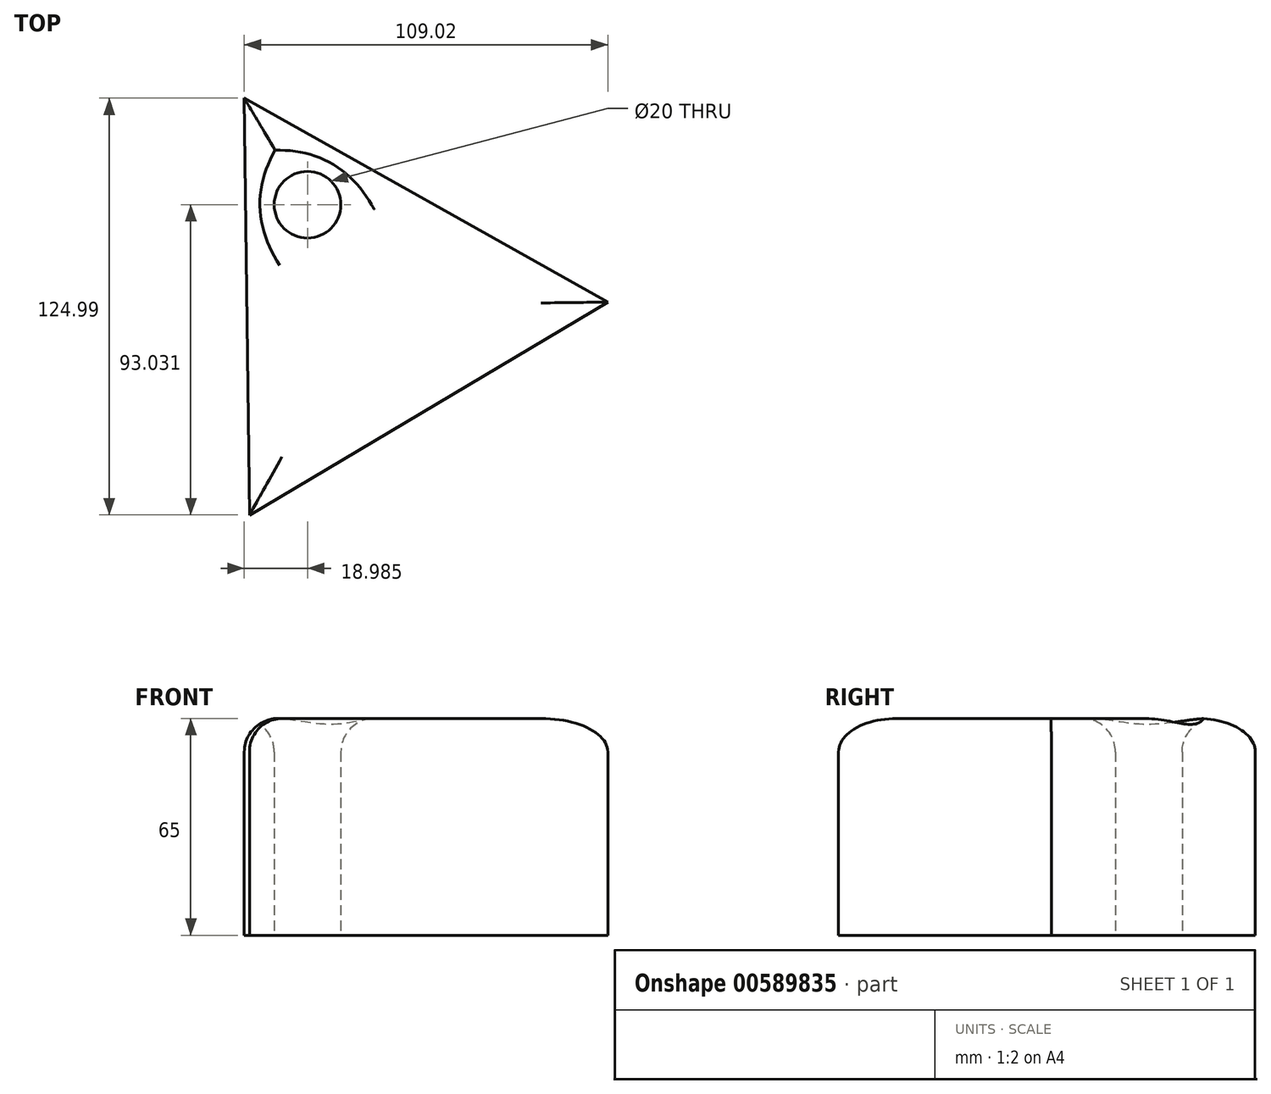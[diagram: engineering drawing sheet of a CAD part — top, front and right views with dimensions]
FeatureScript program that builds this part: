
annotation { "Feature Type Name" : "Feature", "Feature Type Description" : "" }
export const myFeature = defineFeature(function(context is Context, id is Id, definition is map)
    precondition{}
    {
        {
            var Q0;
            Q0=qCreatedBy(makeId("Top.planeOp"),FACE);
            var sketch = newSketch(context, id + "F0", { "sketchPlane" : qUnion([Q0])});
            skCircle(sketch, "E0.cCircle", {"center": v(0, 0) * mm, "radius": 36.08 * mm, "construction": true});
            skLineSegment(sketch, "E0.0", {"start": v(72.16, 0.9) * mm, "end": v(-35.3, -62.94) * mm});
            skLineSegment(sketch, "E0.1", {"start": v(-35.3, -62.94) * mm, "end": v(-36.86, 62.05) * mm});
            skLineSegment(sketch, "E0.2", {"start": v(-36.86, 62.05) * mm, "end": v(72.16, 0.9) * mm});
            skPoint(sketch, "E0.0.midPoint", {"position": v(18.43, -31.02) * mm});
            skLineSegment(sketch, "E1", {"start": v(-36.86, 62.05) * mm, "end": v(0, 0) * mm});
            skCircle(sketch, "E2", {"center": v(-17.88, 30.1) * mm, "radius": 10 * mm});
            skLineSegment(sketch, "E3", {"start": v(0, 0) * mm, "end": v(18.43, -31.02) * mm});
            skCircle(sketch, "E4", {"center": v(9.21, -15.51) * mm, "radius": 10 * mm});
            skSolve(sketch);
        }
        {
            var Q0;
            Q0 = qSketchRegion(id + "F0", true);
            extrude(context, id + "F1", {"entities" : qUnion([Q0]), "depth" : 50 * mm, "offsetDistance" : 25 * mm});
        }
        {
            var Q0;
            {var subQ0=sQuery(id+"F0.wireOp",EDGE,"E2");var subQ1=sQuery(id+"F0.wireOp",EDGE,"E1");var subQ2=makeQuery(id+"F0.imprint","INTERSECT",VERTEX,{"disambiguationData":[OD(0.0)],"derivedFrom":[subQ1,subQ0]});Q0=makeQuery(id+"F0.imprint","IMPRINT",FACE,{"disambiguationData":[TD([[makeQuery(id+"F0.imprint","IMPRINT",EDGE,{"disambiguationData":[TD([[subQ2,-1.0]])],"derivedFrom":subQ1}),1.0]])]});}
            var Q1;
            {var subQ0=sQuery(id+"F0.wireOp",EDGE,"E2");var subQ1=sQuery(id+"F0.wireOp",EDGE,"E1");var subQ2=makeQuery(id+"F0.imprint","INTERSECT",VERTEX,{"disambiguationData":[OD(0.0)],"derivedFrom":[subQ1,subQ0]});Q1=makeQuery(id+"F0.imprint","IMPRINT",FACE,{"disambiguationData":[TD([[makeQuery(id+"F0.imprint","IMPRINT",EDGE,{"disambiguationData":[TD([[subQ2,-1.0]])],"derivedFrom":subQ1}),-1.0]])]});}
            var Q2;
            {var subQ0=sQuery(id+"F0.wireOp",EDGE,"E4");var subQ1=sQuery(id+"F0.wireOp",EDGE,"E3");var subQ2=makeQuery(id+"F0.imprint","INTERSECT",VERTEX,{"disambiguationData":[OD(0.0)],"derivedFrom":[subQ1,subQ0]});Q2=makeQuery(id+"F0.imprint","IMPRINT",FACE,{"disambiguationData":[TD([[makeQuery(id+"F0.imprint","IMPRINT",EDGE,{"disambiguationData":[TD([[subQ2,-1.0]])],"derivedFrom":subQ1}),-1.0]])]});}
            var Q3;
            {var subQ0=sQuery(id+"F0.wireOp",EDGE,"E4");var subQ1=sQuery(id+"F0.wireOp",EDGE,"E3");var subQ2=makeQuery(id+"F0.imprint","INTERSECT",VERTEX,{"disambiguationData":[OD(0.0)],"derivedFrom":[subQ1,subQ0]});Q3=makeQuery(id+"F0.imprint","IMPRINT",FACE,{"disambiguationData":[TD([[makeQuery(id+"F0.imprint","IMPRINT",EDGE,{"disambiguationData":[TD([[subQ2,-1.0]])],"derivedFrom":subQ1}),1.0]])]});}
            extrude(context, id + "F2", {"entities" : qUnion([Q0, Q1, Q2, Q3]), "operationType" : NewBodyOperationType.ADD, "depth" : 65 * mm, "offsetDistance" : 25 * mm});
        }
        {
            var Q0;
            Q0=makeQuery(id+"F2.opExtrude","CAP_FACE",FACE,{"disambiguationData":[OSD([sQuery(id+"F0.wireOp",EDGE,"E2")])],"isStart":false});
            var Q1;
            Q1=makeQuery(id+"F2.opExtrude","CAP_EDGE",EDGE,{"disambiguationData":[OSD([sQuery(id+"F0.wireOp",EDGE,"E4")])],"isStart":false});
            fillet(context, id + "F3", {"entities" : qUnion([Q0, Q1]), "radius" : 10 * mm, "tangentPropagation" : true, "allowEdgeOverflow" : false});
        }
    });
